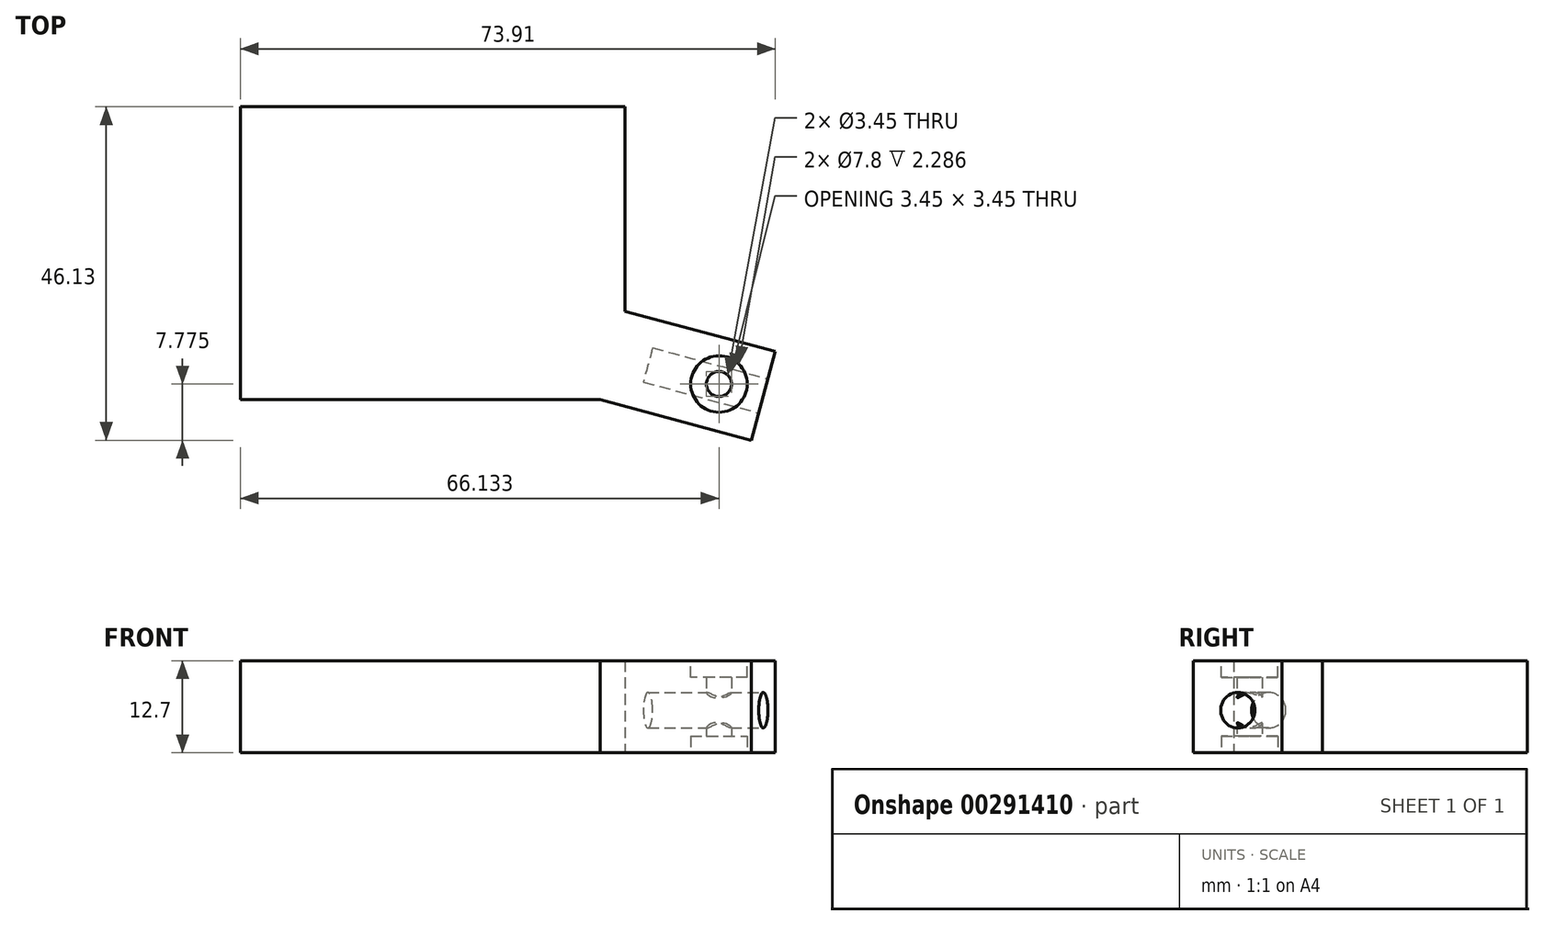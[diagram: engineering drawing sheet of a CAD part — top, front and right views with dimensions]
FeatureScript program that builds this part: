
annotation { "Feature Type Name" : "Feature", "Feature Type Description" : "" }
export const myFeature = defineFeature(function(context is Context, id is Id, definition is map)
    precondition{}
    {
        {
            var Q0;
            Q0=qCreatedBy(makeId("Top.planeOp"),FACE);
            var sketch = newSketch(context, id + "F0", { "sketchPlane" : qUnion([Q0])});
            skLineSegment(sketch, "E0", {"start": v(-12.24, 4.37) * mm, "end": v(40.9, 4.37) * mm});
            skLineSegment(sketch, "E1.bottom", {"start": v(-12.24, 4.37) * mm, "end": v(-12.24, 4.37) * mm});
            skLineSegment(sketch, "E1.top", {"start": v(-12.24, -11.66) * mm, "end": v(-12.24, -11.66) * mm});
            skLineSegment(sketch, "E1.left", {"start": v(-12.24, 4.37) * mm, "end": v(-12.24, -11.66) * mm});
            skLineSegment(sketch, "E1.right", {"start": v(-12.24, 4.37) * mm, "end": v(-12.24, -11.66) * mm});
            skLineSegment(sketch, "E2.bottom", {"start": v(40.9, 4.37) * mm, "end": v(40.9, 4.37) * mm});
            skLineSegment(sketch, "E2.top", {"start": v(40.9, -11.66) * mm, "end": v(40.9, -11.66) * mm});
            skLineSegment(sketch, "E2.left", {"start": v(40.9, 4.37) * mm, "end": v(40.9, -11.66) * mm});
            skLineSegment(sketch, "E2.right", {"start": v(40.9, 4.37) * mm, "end": v(40.9, -11.66) * mm});
            skLineSegment(sketch, "E3", {"start": v(37.46, -36.16) * mm, "end": v(-1.65, -36.16) * mm});
            skLineSegment(sketch, "E4", {"start": v(-12.24, -11.66) * mm, "end": v(-12.24, -36.16) * mm});
            skLineSegment(sketch, "E5", {"start": v(-12.24, -36.16) * mm, "end": v(-1.65, -36.16) * mm});
            skCircle(sketch, "E6", {"center": v(53.9, -33.99) * mm, "radius": 1.73 * mm});
            skPoint(sketch, "E7.end.orphan", {"position": v(49.82, -36.16) * mm});
            skLineSegment(sketch, "E8", {"start": v(40.9, -23.93) * mm, "end": v(40.9, -11.66) * mm});
            skLineSegment(sketch, "E9", {"start": v(40.9, -23.93) * mm, "end": v(61.67, -29.5) * mm});
            skLineSegment(sketch, "E10", {"start": v(61.67, -29.5) * mm, "end": v(58.38, -41.76) * mm});
            skLineSegment(sketch, "E11", {"start": v(58.38, -41.76) * mm, "end": v(47.22, -38.77) * mm});
            skLineSegment(sketch, "E12", {"start": v(37.46, -36.16) * mm, "end": v(47.22, -38.77) * mm});
            skSolve(sketch);
        }
        {
            var Q0;
            Q0=makeQuery(id+"F0.imprint","IMPRINT",FACE,{"disambiguationData":[TD([[makeQuery(id+"F0.imprint","IMPRINT",EDGE,{"derivedFrom":sQuery(id+"F0.wireOp",EDGE,"E0")}),-1.0]])]});
            extrude(context, id + "F1", {"entities" : qUnion([Q0]), "depth" : 12.7 * mm});
        }
        {
            var Q0;
            Q0=makeQuery(id+"F1.opExtrude","SWEPT_FACE",FACE,{"disambiguationData":[OSD([sQuery(id+"F0.wireOp",EDGE,"E10")])]});
            var sketch = newSketch(context, id + "F2", { "sketchPlane" : qUnion([Q0])});
            skCircle(sketch, "E13", {"center": v(-18.88, 5.87) * mm, "radius": 2.45 * mm});
            skPoint(sketch, "E13.centerSnap0", {"position": v(-18.88, 12.7) * mm});
            skSolve(sketch);
        }
        {
            var Q0;
            Q0=makeQuery(id+"F2.imprint","IMPRINT",FACE,{"disambiguationData":[TD([[makeQuery(id+"F2.imprint","IMPRINT",EDGE,{"derivedFrom":sQuery(id+"F2.wireOp",EDGE,"E13")}),1.0]])]});
            extrude(context, id + "F3", {"entities" : qUnion([Q0]), "operationType" : NewBodyOperationType.REMOVE, "oppositeDirection" : true, "depth" : 16.5 * mm});
        }
        {
            var Q0;
            Q0=makeQuery(id+"F1.opExtrude","CAP_FACE",FACE,{"disambiguationData":[OSD([sQuery(id+"F0.wireOp",EDGE,"E0"),sQuery(id+"F0.wireOp",EDGE,"E1.right"),sQuery(id+"F0.wireOp",EDGE,"E2.right"),sQuery(id+"F0.wireOp",EDGE,"E3"),sQuery(id+"F0.wireOp",EDGE,"E4"),sQuery(id+"F0.wireOp",EDGE,"E5"),sQuery(id+"F0.wireOp",EDGE,"E6"),sQuery(id+"F0.wireOp",EDGE,"E8"),sQuery(id+"F0.wireOp",EDGE,"E9"),sQuery(id+"F0.wireOp",EDGE,"E10"),sQuery(id+"F0.wireOp",EDGE,"E11"),sQuery(id+"F0.wireOp",EDGE,"E12")])],"isStart":false});
            var sketch = newSketch(context, id + "F4", { "sketchPlane" : qUnion([Q0])});
            skCircle(sketch, "E14", {"center": v(53.9, -33.99) * mm, "radius": 3.9 * mm});
            skSolve(sketch);
        }
        {
            var Q0;
            Q0=makeQuery(id+"F4.imprint","IMPRINT",FACE,{"disambiguationData":[TD([[makeQuery(id+"F4.imprint","IMPRINT",EDGE,{"derivedFrom":sQuery(id+"F4.wireOp",EDGE,"E14")}),1.0]])]});
            extrude(context, id + "F5", {"entities" : qUnion([Q0]), "operationType" : NewBodyOperationType.REMOVE, "oppositeDirection" : true, "depth" : 2.3 * mm});
        }
        {
            var Q0;
            Q0=makeQuery(id+"F1.opExtrude","CAP_FACE",FACE,{"disambiguationData":[OSD([sQuery(id+"F0.wireOp",EDGE,"E0"),sQuery(id+"F0.wireOp",EDGE,"E1.right"),sQuery(id+"F0.wireOp",EDGE,"E2.right"),sQuery(id+"F0.wireOp",EDGE,"E3"),sQuery(id+"F0.wireOp",EDGE,"E4"),sQuery(id+"F0.wireOp",EDGE,"E5"),sQuery(id+"F0.wireOp",EDGE,"E6"),sQuery(id+"F0.wireOp",EDGE,"E8"),sQuery(id+"F0.wireOp",EDGE,"E9"),sQuery(id+"F0.wireOp",EDGE,"E10"),sQuery(id+"F0.wireOp",EDGE,"E11"),sQuery(id+"F0.wireOp",EDGE,"E12")])],"isStart":true});
            var sketch = newSketch(context, id + "F6", { "sketchPlane" : qUnion([Q0])});
            skCircle(sketch, "E15", {"center": v(53.9, 33.99) * mm, "radius": 3.9 * mm});
            skSolve(sketch);
        }
        {
            var Q0;
            Q0=makeQuery(id+"F6.imprint","IMPRINT",FACE,{"disambiguationData":[TD([[makeQuery(id+"F6.imprint","IMPRINT",EDGE,{"derivedFrom":sQuery(id+"F6.wireOp",EDGE,"E15")}),1.0]])]});
            extrude(context, id + "F7", {"entities" : qUnion([Q0]), "operationType" : NewBodyOperationType.REMOVE, "oppositeDirection" : true, "depth" : 2.3 * mm});
        }
    });
